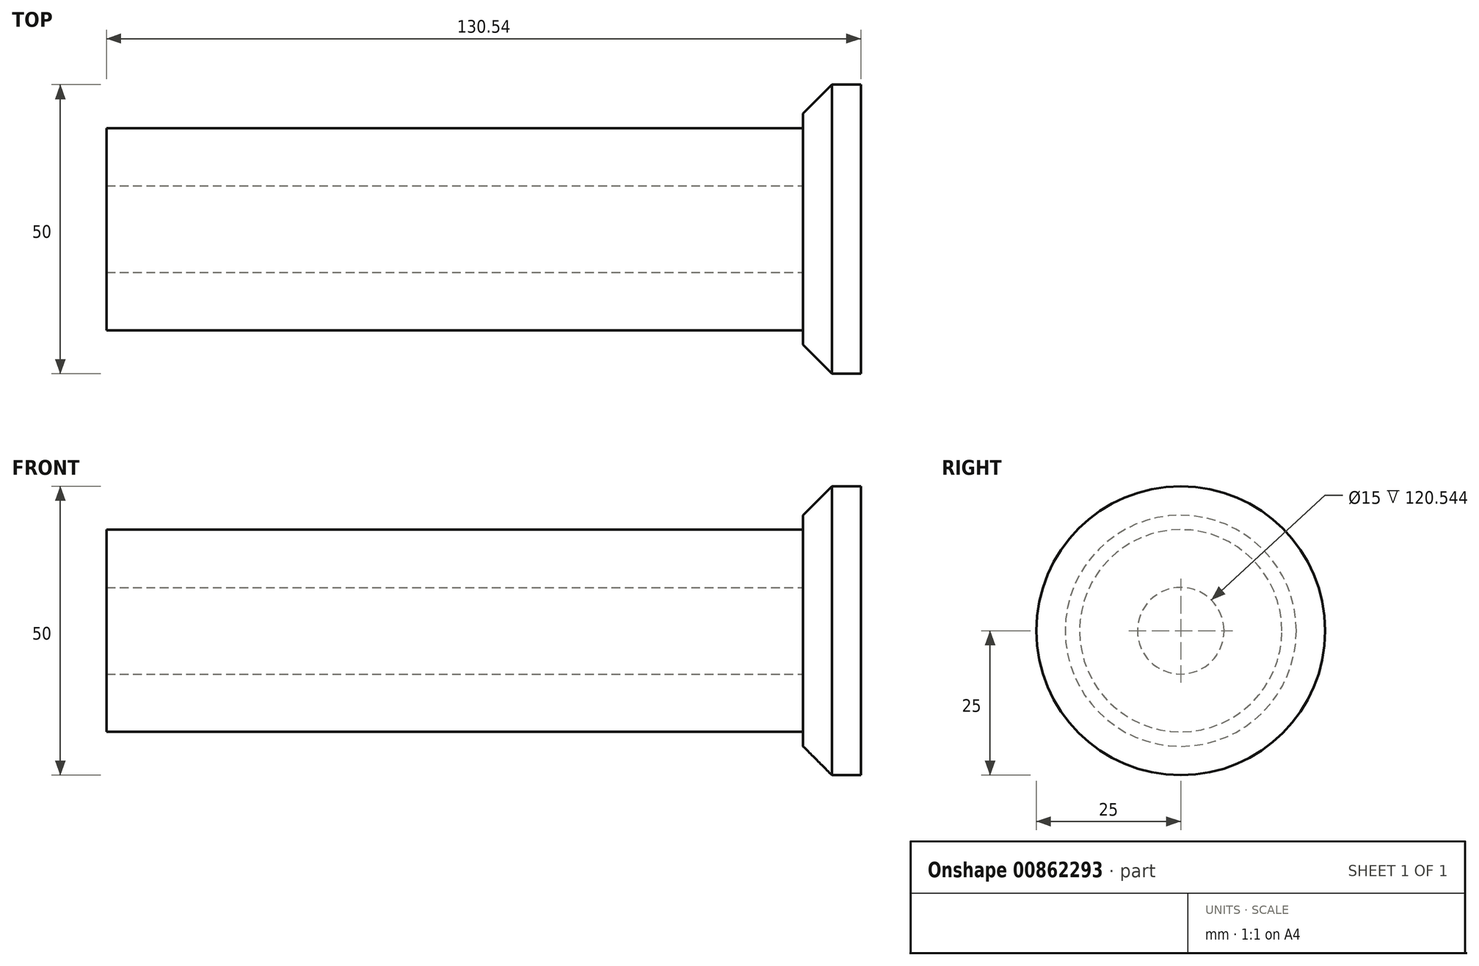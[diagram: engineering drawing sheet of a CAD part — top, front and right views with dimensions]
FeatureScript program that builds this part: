
annotation { "Feature Type Name" : "Feature", "Feature Type Description" : "" }
export const myFeature = defineFeature(function(context is Context, id is Id, definition is map)
    precondition{}
    {
        {
            var Q0;
            Q0=qCreatedBy(makeId("Front.planeOp"),FACE);
            var sketch = newSketch(context, id + "F0", { "sketchPlane" : qUnion([Q0])});
            skLineSegment(sketch, "E0.bottom", {"start": v(12.77, -5) * mm, "end": v(-12.77, -5) * mm});
            skLineSegment(sketch, "E0.top", {"start": v(12.77, 5) * mm, "end": v(-12.77, 5) * mm});
            skLineSegment(sketch, "E0.left", {"start": v(12.77, -5) * mm, "end": v(12.77, 5) * mm});
            skLineSegment(sketch, "E0.right", {"start": v(-12.77, -5) * mm, "end": v(-12.77, 5) * mm});
            skPoint(sketch, "E0.middle", {"position": v(0, 0) * mm});
            skLineSegment(sketch, "E1.bottom", {"start": v(17.77, 12.5) * mm, "end": v(7.77, 12.5) * mm});
            skLineSegment(sketch, "E1.top", {"start": v(17.77, -12.5) * mm, "end": v(7.77, -12.5) * mm});
            skLineSegment(sketch, "E1.left", {"start": v(17.77, 12.5) * mm, "end": v(17.77, -12.5) * mm});
            skLineSegment(sketch, "E1.right", {"start": v(7.77, 12.5) * mm, "end": v(7.77, -12.5) * mm});
            skPoint(sketch, "E1.middle", {"position": v(12.77, 0) * mm});
            skSolve(sketch);
        }
        {
            var Q0;
            Q0 = qSketchRegion(id + "F0", true);
            var Q1;
            Q1=sQuery(id+"F0.wireOp",EDGE,"E1.bottom");
            revolve(context, id + "F1", {"surfaceOperationType" : NewSurfaceOperationType.NEW, "entities" : qUnion([Q0]), "axis" : qUnion([Q1]), "revolveType" : RevolveType.FULL});
        }
        {
            var Q0;
            Q0=makeQuery(id+"F1.opRevolve","SWEPT_EDGE",EDGE,{"disambiguationData":[OSD([sQuery(id+"F0.wireOp",EDGE,"E1.top"),sQuery(id+"F0.wireOp",EDGE,"E1.right")])]});
            chamfer(context, id + "F2", {"entities" : qUnion([Q0]), "width" : 5 * mm, "tangentPropagation" : true});
        }
        {
            var Q0;
            Q0=makeQuery(id+"F1.opRevolve","SWEPT_FACE",FACE,{"disambiguationData":[OSD([sQuery(id+"F0.wireOp",EDGE,"E0.right")])]});
            extrude(context, id + "F3", {"entities" : qUnion([Q0]), "operationType" : NewBodyOperationType.ADD, "depth" : 100 * mm, "offsetDistance" : 25 * mm});
        }
    });
